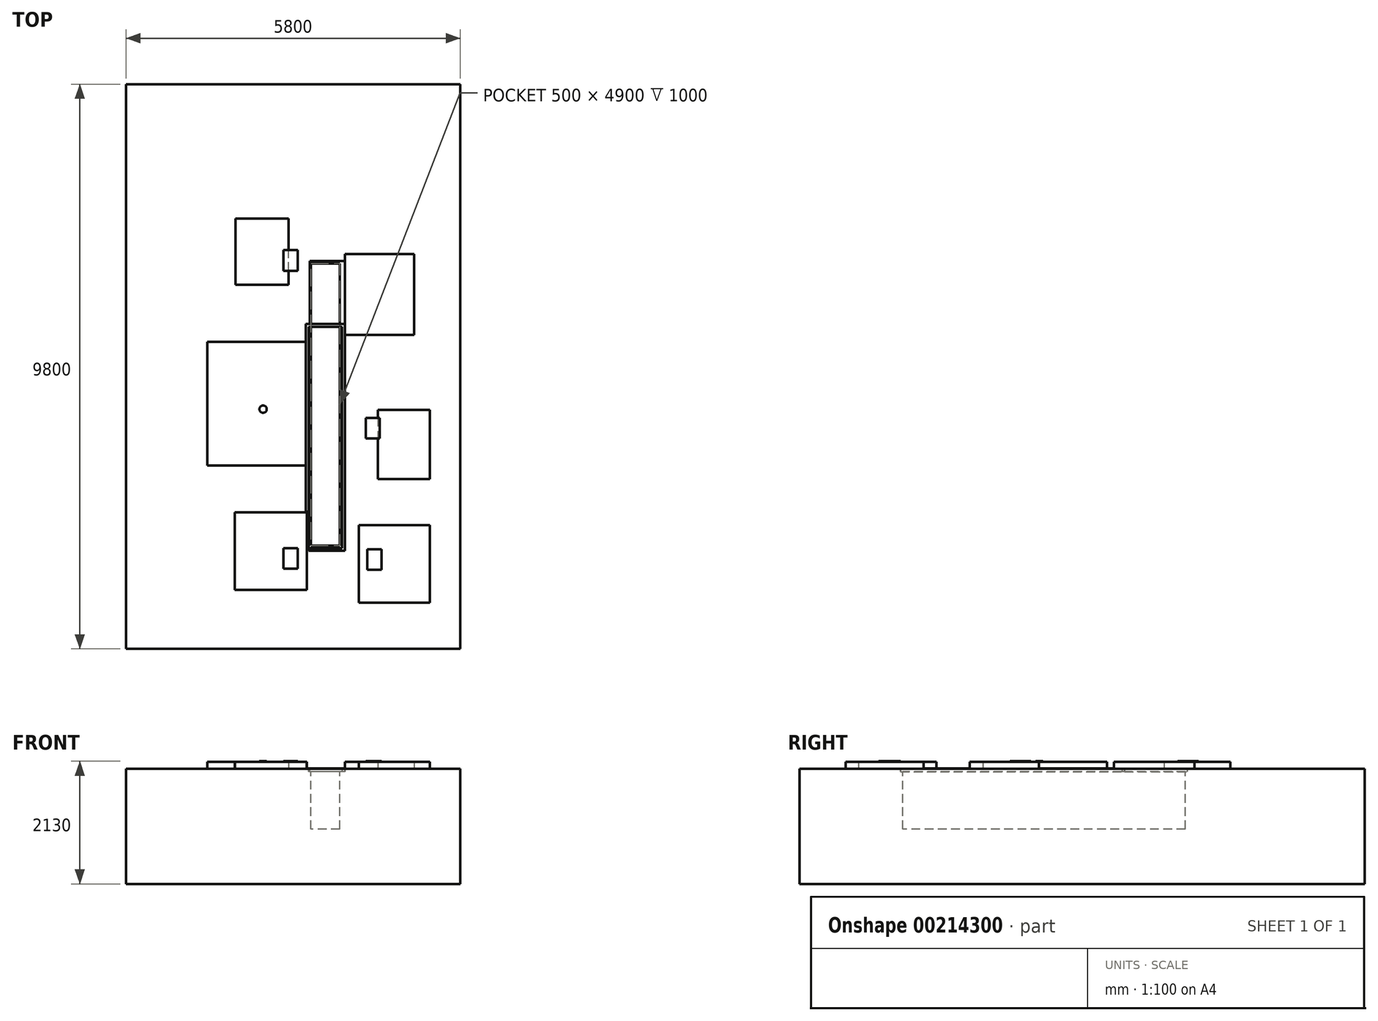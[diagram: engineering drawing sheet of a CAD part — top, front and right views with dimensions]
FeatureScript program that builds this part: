
annotation { "Feature Type Name" : "Feature", "Feature Type Description" : "" }
export const myFeature = defineFeature(function(context is Context, id is Id, definition is map)
    precondition{}
    {
        {
            var Q0;
            Q0=qCreatedBy(makeId("Top.planeOp"),FACE);
            var sketch = newSketch(context, id + "F0", { "sketchPlane" : qUnion([Q0])});
            skLineSegment(sketch, "E0.bottom", {"start": v(2900, -4900) * mm, "end": v(-2900, -4900) * mm});
            skLineSegment(sketch, "E0.top", {"start": v(2900, 4900) * mm, "end": v(-2900, 4900) * mm});
            skLineSegment(sketch, "E0.left", {"start": v(2900, -4900) * mm, "end": v(2900, 4900) * mm});
            skLineSegment(sketch, "E0.right", {"start": v(-2900, -4900) * mm, "end": v(-2900, 4900) * mm});
            skPoint(sketch, "E0.middle", {"position": v(0, 0) * mm});
            skSolve(sketch);
        }
        {
            var Q0;
            Q0 = qSketchRegion(id + "F0", true);
            extrude(context, id + "F1", {"entities" : qUnion([Q0]), "oppositeDirection" : true, "depth" : 2000 * mm});
        }
        {
            var Q0;
            Q0=makeQuery(id+"F1.opExtrude","CAP_FACE",FACE,{"disambiguationData":[OSD([sQuery(id+"F0.wireOp",EDGE,"E0.bottom"),sQuery(id+"F0.wireOp",EDGE,"E0.top"),sQuery(id+"F0.wireOp",EDGE,"E0.left"),sQuery(id+"F0.wireOp",EDGE,"E0.right")])],"isStart":true});
            var sketch = newSketch(context, id + "F2", { "sketchPlane" : qUnion([Q0])});
            skLineSegment(sketch, "E1.bottom", {"start": v(-80, 1420) * mm, "end": v(-1000, 1420) * mm});
            skLineSegment(sketch, "E1.top", {"start": v(-80, 2570) * mm, "end": v(-1000, 2570) * mm});
            skLineSegment(sketch, "E1.left", {"start": v(-80, 1420) * mm, "end": v(-80, 2570) * mm});
            skLineSegment(sketch, "E1.right", {"start": v(-1000, 1420) * mm, "end": v(-1000, 2570) * mm});
            skPoint(sketch, "E1.middle", {"position": v(-540, 1995) * mm});
            skLineSegment(sketch, "E2.bottom", {"start": v(2100, 550) * mm, "end": v(900, 550) * mm});
            skLineSegment(sketch, "E2.top", {"start": v(2100, 1950) * mm, "end": v(900, 1950) * mm});
            skLineSegment(sketch, "E2.left", {"start": v(2100, 550) * mm, "end": v(2100, 1950) * mm});
            skLineSegment(sketch, "E2.right", {"start": v(900, 550) * mm, "end": v(900, 1950) * mm});
            skPoint(sketch, "E2.middle", {"position": v(1500, 1250) * mm});
            skLineSegment(sketch, "E3.bottom", {"start": v(900, 740) * mm, "end": v(290, 740) * mm});
            skLineSegment(sketch, "E3.top", {"start": v(900, 1830) * mm, "end": v(290, 1830) * mm});
            skLineSegment(sketch, "E3.left", {"start": v(900, 740) * mm, "end": v(900, 1830) * mm});
            skLineSegment(sketch, "E3.right", {"start": v(290, 740) * mm, "end": v(290, 1830) * mm});
            skPoint(sketch, "E3.middle", {"position": v(595, 1285) * mm});
            skLineSegment(sketch, "E4.bottom", {"start": v(900, 740) * mm, "end": v(220, 740) * mm});
            skLineSegment(sketch, "E4.top", {"start": v(900, -3200) * mm, "end": v(270, -3200) * mm});
            skLineSegment(sketch, "E4.left", {"start": v(900, 740) * mm, "end": v(900, -3200) * mm});
            skLineSegment(sketch, "E4.right", {"start": v(220, 740) * mm, "end": v(220, -2515) * mm});
            skLineSegment(sketch, "E5.0", {"start": v(270, 690) * mm, "end": v(270, -3150) * mm});
            skLineSegment(sketch, "E5.1", {"start": v(850, 690) * mm, "end": v(270, 690) * mm});
            skLineSegment(sketch, "E5.2", {"start": v(850, 690) * mm, "end": v(850, -3150) * mm});
            skLineSegment(sketch, "E5.3", {"start": v(850, -3150) * mm, "end": v(270, -3150) * mm});
            skLineSegment(sketch, "E6.bottom", {"start": v(1470, -750) * mm, "end": v(2370, -750) * mm});
            skLineSegment(sketch, "E6.top", {"start": v(1470, -1950) * mm, "end": v(2370, -1950) * mm});
            skLineSegment(sketch, "E6.left", {"start": v(1470, -750) * mm, "end": v(1470, -1950) * mm});
            skLineSegment(sketch, "E6.right", {"start": v(2370, -750) * mm, "end": v(2370, -1950) * mm});
            skLineSegment(sketch, "E7.bottom", {"start": v(1140, -2750) * mm, "end": v(2370, -2750) * mm});
            skLineSegment(sketch, "E7.top", {"start": v(1140, -4100) * mm, "end": v(2370, -4100) * mm});
            skLineSegment(sketch, "E7.left", {"start": v(1140, -2750) * mm, "end": v(1140, -4100) * mm});
            skLineSegment(sketch, "E7.right", {"start": v(2370, -2750) * mm, "end": v(2370, -4100) * mm});
            skLineSegment(sketch, "E8", {"start": v(220, -2515) * mm, "end": v(270, -2515) * mm});
            skLineSegment(sketch, "E9", {"start": v(270, -3150) * mm, "end": v(270, -3200) * mm});
            skLineSegment(sketch, "E10.bottom", {"start": v(-1490, 430) * mm, "end": v(220, 430) * mm});
            skLineSegment(sketch, "E10.top", {"start": v(-1490, -1720) * mm, "end": v(220, -1720) * mm});
            skLineSegment(sketch, "E10.left", {"start": v(-1490, 430) * mm, "end": v(-1490, -1720) * mm});
            skLineSegment(sketch, "E10.right", {"start": v(220, 430) * mm, "end": v(220, -1720) * mm});
            skLineSegment(sketch, "E11.bottom", {"start": v(-1010, -2530) * mm, "end": v(240, -2530) * mm});
            skLineSegment(sketch, "E11.top", {"start": v(-1010, -3880) * mm, "end": v(240, -3880) * mm});
            skLineSegment(sketch, "E11.left", {"start": v(-1010, -2530) * mm, "end": v(-1010, -3880) * mm});
            skLineSegment(sketch, "E11.right", {"start": v(240, -2530) * mm, "end": v(240, -3880) * mm});
            skSolve(sketch);
        }
        {
            var Q0;
            Q0=makeQuery(id+"F2.imprint","IMPRINT",FACE,{"disambiguationData":[TD([[makeQuery(id+"F2.imprint","IMPRINT",EDGE,{"derivedFrom":sQuery(id+"F2.wireOp",EDGE,"E1.bottom")}),-1.0]])]});
            var Q1;
            Q1=makeQuery(id+"F2.imprint","IMPRINT",FACE,{"disambiguationData":[TD([[makeQuery(id+"F2.imprint","IMPRINT",EDGE,{"derivedFrom":sQuery(id+"F2.wireOp",EDGE,"E6.bottom")}),-1.0]])]});
            var Q2;
            Q2=makeQuery(id+"F2.imprint","IMPRINT",FACE,{"disambiguationData":[TD([[makeQuery(id+"F2.imprint","IMPRINT",EDGE,{"derivedFrom":sQuery(id+"F2.wireOp",EDGE,"E7.bottom")}),-1.0]])]});
            var Q3;
            Q3=makeQuery(id+"F2.imprint","IMPRINT",FACE,{"disambiguationData":[TD([[makeQuery(id+"F2.imprint","IMPRINT",EDGE,{"derivedFrom":sQuery(id+"F2.wireOp",EDGE,"E10.bottom")}),-1.0]])]});
            var Q4;
            Q4=makeQuery(id+"F2.imprint","IMPRINT",FACE,{"disambiguationData":[TD([[makeQuery(id+"F2.imprint","IMPRINT",EDGE,{"derivedFrom":sQuery(id+"F2.wireOp",EDGE,"E11.bottom")}),-1.0]])]});
            var Q5;
            {var subQ1=sQuery(id+"F2.wireOp",EDGE,"E2.bottom");Q5=makeQuery(id+"F2.imprint","IMPRINT",FACE,{"disambiguationData":[TD([[makeQuery(id+"F2.imprint","IMPRINT",EDGE,{"derivedFrom":subQ1}),-1.0]])]});}
            extrude(context, id + "F3", {"entities" : qUnion([Q0, Q1, Q2, Q3, Q4, Q5]), "operationType" : NewBodyOperationType.ADD, "depth" : 120 * mm});
        }
        {
            var Q0;
            {var subQ4=sQuery(id+"F2.wireOp",EDGE,"E4.top");Q0=makeQuery(id+"F2.imprint","IMPRINT",FACE,{"disambiguationData":[TD([[makeQuery(id+"F2.imprint","IMPRINT",EDGE,{"derivedFrom":subQ4}),-1.0]])]});}
            extrude(context, id + "F4", {"entities" : qUnion([Q0]), "operationType" : NewBodyOperationType.ADD, "depth" : 5 * mm});
        }
        {
            var Q0;
            Q0=makeQuery(id+"F1.opExtrude","CAP_FACE",FACE,{"disambiguationData":[OSD([sQuery(id+"F0.wireOp",EDGE,"E0.bottom"),sQuery(id+"F0.wireOp",EDGE,"E0.top"),sQuery(id+"F0.wireOp",EDGE,"E0.left"),sQuery(id+"F0.wireOp",EDGE,"E0.right")])],"isStart":true});
            var sketch = newSketch(context, id + "F5", { "sketchPlane" : qUnion([Q0])});
            skLineSegment(sketch, "E12.0", {"start": v(270, 690) * mm, "end": v(270, -2515) * mm});
            skLineSegment(sketch, "E13.0", {"start": v(850, -3150) * mm, "end": v(270, -3150) * mm});
            skLineSegment(sketch, "E14.0", {"start": v(850, 690) * mm, "end": v(850, -3150) * mm});
            skLineSegment(sketch, "E15.0", {"start": v(850, 690) * mm, "end": v(270, 690) * mm});
            skLineSegment(sketch, "E16", {"start": v(270, -3150) * mm, "end": v(270, -2515) * mm});
            skLineSegment(sketch, "E17.bottom", {"start": v(900, 740) * mm, "end": v(290, 740) * mm});
            skLineSegment(sketch, "E17.top", {"start": v(900, 1830) * mm, "end": v(290, 1830) * mm});
            skLineSegment(sketch, "E17.left", {"start": v(900, 740) * mm, "end": v(900, 1830) * mm});
            skLineSegment(sketch, "E17.right", {"start": v(290, 740) * mm, "end": v(290, 1830) * mm});
            skSolve(sketch);
        }
        {
            var Q0;
            Q0 = qSketchRegion(id + "F5", true);
            extrude(context, id + "F6", {"entities" : qUnion([Q0]), "operationType" : NewBodyOperationType.REMOVE, "oppositeDirection" : true, "depth" : 50 * mm});
        }
        {
            var Q0;
            Q0=makeQuery(id+"F6.boolean.opBoolean","COPY",FACE,{"derivedFrom":makeQuery(id+"F6.opExtrude","CAP_FACE",FACE,{"disambiguationData":[OSD([sQuery(id+"F5.wireOp",EDGE,"E12.0"),sQuery(id+"F5.wireOp",EDGE,"E13.0"),sQuery(id+"F5.wireOp",EDGE,"E14.0"),sQuery(id+"F5.wireOp",EDGE,"E15.0"),sQuery(id+"F5.wireOp",EDGE,"E16")])],"isStart":false})});
            var sketch = newSketch(context, id + "F7", { "sketchPlane" : qUnion([Q0])});
            skLineSegment(sketch, "E18.0", {"start": v(310, 650) * mm, "end": v(310, -2515) * mm});
            skLineSegment(sketch, "E18.1", {"start": v(810, 650) * mm, "end": v(310, 650) * mm});
            skLineSegment(sketch, "E18.2", {"start": v(310, -3110) * mm, "end": v(310, -2515) * mm});
            skLineSegment(sketch, "E18.3", {"start": v(810, -3110) * mm, "end": v(310, -3110) * mm});
            skLineSegment(sketch, "E18.4", {"start": v(810, 650) * mm, "end": v(810, -3110) * mm});
            skPoint(sketch, "E19.orphan", {"position": v(220, 740) * mm});
            skPoint(sketch, "E20.orphan", {"position": v(900, 550) * mm});
            skPoint(sketch, "E21.orphan", {"position": v(900, 1950) * mm});
            skLineSegment(sketch, "E22.bottom", {"start": v(310, 1790) * mm, "end": v(810, 1790) * mm});
            skLineSegment(sketch, "E22.top", {"start": v(310, 780) * mm, "end": v(810, 780) * mm});
            skLineSegment(sketch, "E22.left", {"start": v(310, 1790) * mm, "end": v(310, 780) * mm});
            skLineSegment(sketch, "E22.right", {"start": v(810, 1790) * mm, "end": v(810, 780) * mm});
            skPoint(sketch, "E23.0.end.orphan", {"position": v(900, 1830) * mm});
            skPoint(sketch, "E24.0.start.orphan", {"position": v(900, 740) * mm});
            skPoint(sketch, "E25.0.end.orphan", {"position": v(290, 1830) * mm});
            skPoint(sketch, "E25.0.start.orphan", {"position": v(290, 740) * mm});
            skSolve(sketch);
        }
        {
            var Q0;
            Q0 = qSketchRegion(id + "F7", true);
            extrude(context, id + "F8", {"entities" : qUnion([Q0]), "operationType" : NewBodyOperationType.REMOVE, "oppositeDirection" : true, "depth" : 1000 * mm});
        }
        {
            var Q0;
            Q0=makeQuery(id+"F8.boolean.opBoolean","COPY",FACE,{"derivedFrom":makeQuery(id+"F8.opExtrude","SWEPT_FACE",FACE,{"disambiguationData":[OSD([sQuery(id+"F7.wireOp",EDGE,"E18.1")])]})});
            var sketch = newSketch(context, id + "F9", { "sketchPlane" : qUnion([Q0])});
            skLineSegment(sketch, "E26.0", {"start": v(810, -1050) * mm, "end": v(310, -1050) * mm});
            skLineSegment(sketch, "E27.0", {"start": v(310, -1050) * mm, "end": v(310, -50) * mm});
            skLineSegment(sketch, "E28.0", {"start": v(810, -50) * mm, "end": v(310, -50) * mm});
            skLineSegment(sketch, "E29.0", {"start": v(810, -1050) * mm, "end": v(810, -50) * mm});
            skSolve(sketch);
        }
        {
            var Q0;
            Q0 = qSketchRegion(id + "F9", true);
            extrude(context, id + "F10", {"entities" : qUnion([Q0]), "operationType" : NewBodyOperationType.REMOVE, "oppositeDirection" : true, "depth" : 290 * mm});
        }
        {
            var Q0;
            Q0=makeQuery(id+"F3.opExtrude","CAP_FACE",FACE,{"disambiguationData":[OSD([sQuery(id+"F2.wireOp",EDGE,"E1.bottom"),sQuery(id+"F2.wireOp",EDGE,"E1.top"),sQuery(id+"F2.wireOp",EDGE,"E1.left"),sQuery(id+"F2.wireOp",EDGE,"E1.right")])],"isStart":false});
            var sketch = newSketch(context, id + "F11", { "sketchPlane" : qUnion([Q0])});
            skLineSegment(sketch, "E30.bottom", {"start": v(80, 2020) * mm, "end": v(-165, 2020) * mm});
            skLineSegment(sketch, "E30.top", {"start": v(80, 1660) * mm, "end": v(-165, 1660) * mm});
            skLineSegment(sketch, "E30.left", {"start": v(80, 2020) * mm, "end": v(80, 1660) * mm});
            skLineSegment(sketch, "E30.right", {"start": v(-165, 2020) * mm, "end": v(-165, 1660) * mm});
            skPoint(sketch, "E30.middle", {"position": v(-42.5, 1840) * mm});
            skCircle(sketch, "E31", {"center": v(-520, -740) * mm, "radius": 63.5 * mm});
            skLineSegment(sketch, "E32.bottom", {"start": v(80, -3150) * mm, "end": v(-165, -3150) * mm});
            skLineSegment(sketch, "E32.top", {"start": v(80, -3510) * mm, "end": v(-165, -3510) * mm});
            skLineSegment(sketch, "E32.left", {"start": v(80, -3150) * mm, "end": v(80, -3510) * mm});
            skLineSegment(sketch, "E32.right", {"start": v(-165, -3150) * mm, "end": v(-165, -3510) * mm});
            skPoint(sketch, "E32.middle", {"position": v(-42.5, -3330) * mm});
            skLineSegment(sketch, "E33.bottom", {"start": v(1535, -3530) * mm, "end": v(1290, -3530) * mm});
            skLineSegment(sketch, "E33.top", {"start": v(1535, -3170) * mm, "end": v(1290, -3170) * mm});
            skLineSegment(sketch, "E33.left", {"start": v(1535, -3530) * mm, "end": v(1535, -3170) * mm});
            skLineSegment(sketch, "E33.right", {"start": v(1290, -3530) * mm, "end": v(1290, -3170) * mm});
            skPoint(sketch, "E33.middle", {"position": v(1412.5, -3350) * mm});
            skLineSegment(sketch, "E34.bottom", {"start": v(1505, -890) * mm, "end": v(1260, -890) * mm});
            skLineSegment(sketch, "E34.top", {"start": v(1505, -1250) * mm, "end": v(1260, -1250) * mm});
            skLineSegment(sketch, "E34.left", {"start": v(1505, -890) * mm, "end": v(1505, -1250) * mm});
            skLineSegment(sketch, "E34.right", {"start": v(1260, -890) * mm, "end": v(1260, -1250) * mm});
            skPoint(sketch, "E34.middle", {"position": v(1382.5, -1070) * mm});
            skSolve(sketch);
        }
        {
            var Q0;
            Q0 = qSketchRegion(id + "F11", true);
            extrude(context, id + "F12", {"entities" : qUnion([Q0]), "operationType" : NewBodyOperationType.ADD, "depth" : 10 * mm});
        }
    });
